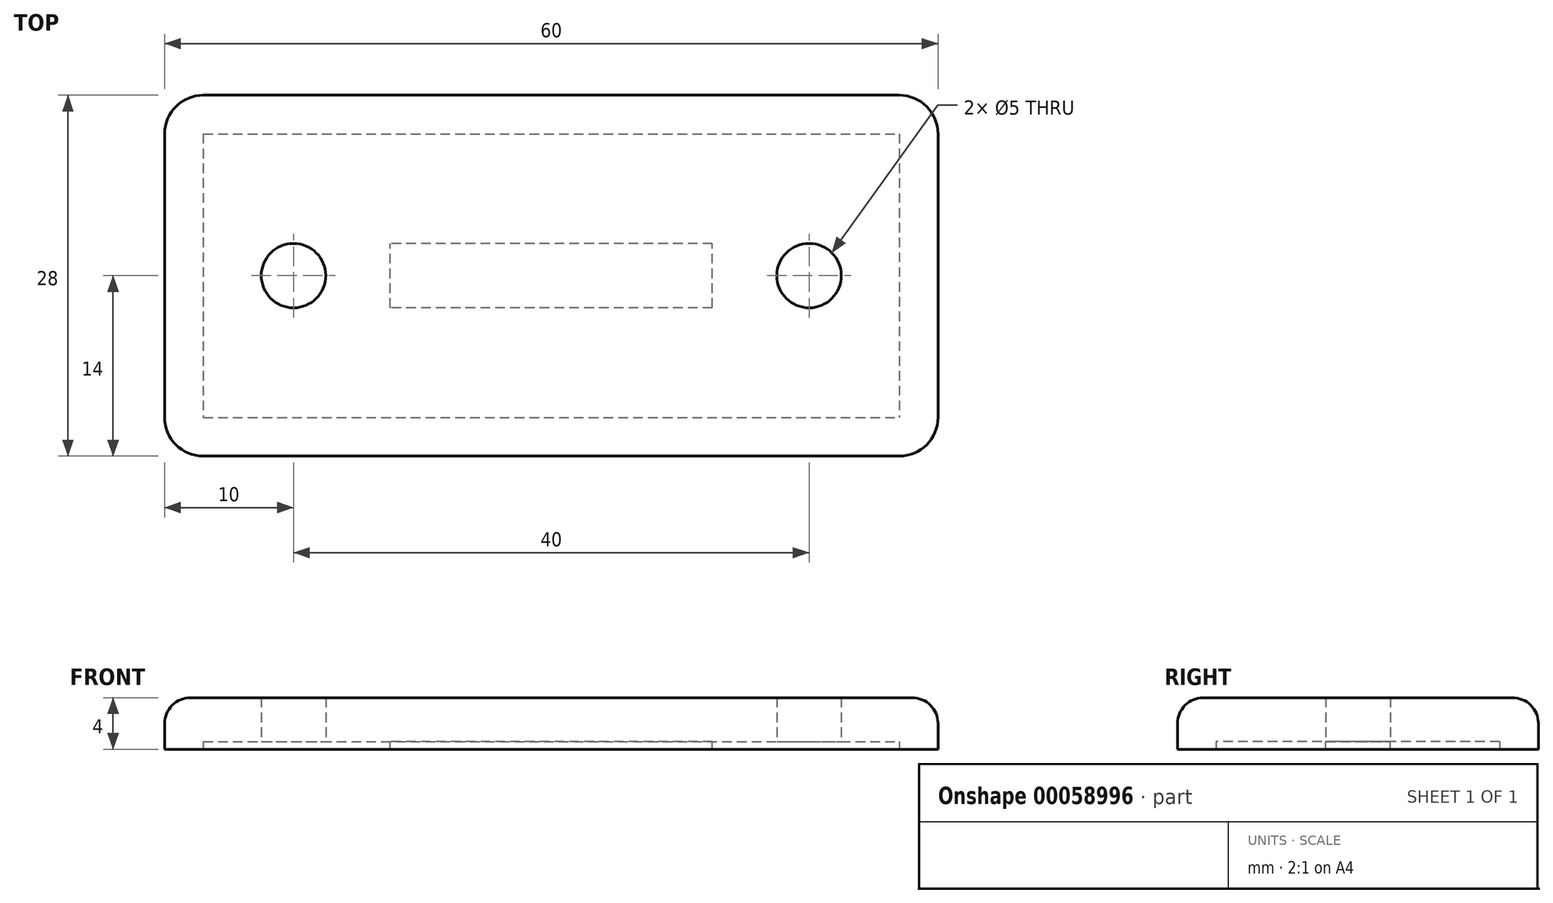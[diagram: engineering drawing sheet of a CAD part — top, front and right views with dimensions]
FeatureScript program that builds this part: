
annotation { "Feature Type Name" : "Feature", "Feature Type Description" : "" }
export const myFeature = defineFeature(function(context is Context, id is Id, definition is map)
    precondition{}
    {
        {
            var Q0;
            Q0=qCreatedBy(makeId("Top.planeOp"),FACE);
            var sketch = newSketch(context, id + "F0", { "sketchPlane" : qUnion([Q0])});
            skLineSegment(sketch, "E0.rect.bottom", {"start": v(-30, 14) * mm, "end": v(30, 14) * mm});
            skLineSegment(sketch, "E0.rect.top", {"start": v(-30, -14) * mm, "end": v(30, -14) * mm});
            skLineSegment(sketch, "E0.rect.left", {"start": v(-30, 14) * mm, "end": v(-30, -14) * mm});
            skLineSegment(sketch, "E0.rect.right", {"start": v(30, 14) * mm, "end": v(30, -14) * mm});
            skPoint(sketch, "E0.rect.middle", {"position": v(0, 0) * mm});
            skCircle(sketch, "E1", {"center": v(-20, 0) * mm, "radius": 2.5 * mm});
            skCircle(sketch, "E2", {"center": v(20, 0) * mm, "radius": 2.5 * mm});
            skSolve(sketch);
        }
        {
            var Q0;
            Q0 = qSketchRegion(id + "F0", true);
            extrude(context, id + "F1", {"entities" : qUnion([Q0]), "depth" : 4 * mm});
        }
        {
            var Q0;
            Q0=makeQuery(id+"F1.opExtrude","CAP_FACE",FACE,{"disambiguationData":[OSD([sQuery(id+"F0.wireOp",EDGE,"E0.rect.bottom"),sQuery(id+"F0.wireOp",EDGE,"E0.rect.top"),sQuery(id+"F0.wireOp",EDGE,"E0.rect.left"),sQuery(id+"F0.wireOp",EDGE,"E0.rect.right"),sQuery(id+"F0.wireOp",EDGE,"E1"),sQuery(id+"F0.wireOp",EDGE,"E2")])],"isStart":true});
            var sketch = newSketch(context, id + "F2", { "sketchPlane" : qUnion([Q0])});
            skLineSegment(sketch, "E3.0", {"start": v(-27, -11) * mm, "end": v(27, -11) * mm});
            skLineSegment(sketch, "E3.1", {"start": v(-27, -11) * mm, "end": v(-27, 11) * mm});
            skLineSegment(sketch, "E3.2", {"start": v(-27, 11) * mm, "end": v(27, 11) * mm});
            skLineSegment(sketch, "E3.3", {"start": v(27, -11) * mm, "end": v(27, 11) * mm});
            skSolve(sketch);
        }
        {
            var Q0;
            Q0 = qSketchRegion(id + "F2", true);
            extrude(context, id + "F3", {"entities" : qUnion([Q0]), "operationType" : NewBodyOperationType.REMOVE, "oppositeDirection" : true, "depth" : 0.6 * mm});
        }
        {
            var Q0;
            Q0=makeQuery(id+"F1.opExtrude","SWEPT_EDGE",EDGE,{"disambiguationData":[OSD([sQuery(id+"F0.wireOp",EDGE,"E0.rect.bottom"),sQuery(id+"F0.wireOp",EDGE,"E0.rect.left")])]});
            var Q1;
            Q1=makeQuery(id+"F1.opExtrude","SWEPT_EDGE",EDGE,{"disambiguationData":[OSD([sQuery(id+"F0.wireOp",EDGE,"E0.rect.top"),sQuery(id+"F0.wireOp",EDGE,"E0.rect.left")])]});
            var Q2;
            Q2=makeQuery(id+"F1.opExtrude","SWEPT_EDGE",EDGE,{"disambiguationData":[OSD([sQuery(id+"F0.wireOp",EDGE,"E0.rect.top"),sQuery(id+"F0.wireOp",EDGE,"E0.rect.right")])]});
            var Q3;
            Q3=makeQuery(id+"F1.opExtrude","SWEPT_EDGE",EDGE,{"disambiguationData":[OSD([sQuery(id+"F0.wireOp",EDGE,"E0.rect.bottom"),sQuery(id+"F0.wireOp",EDGE,"E0.rect.right")])]});
            fillet(context, id + "F4", {"entities" : qUnion([Q0, Q1, Q2, Q3]), "radius" : 3 * mm, "tangentPropagation" : true, "allowEdgeOverflow" : false});
        }
        {
            var Q0;
            Q0=makeQuery(id+"F1.opExtrude","CAP_EDGE",EDGE,{"disambiguationData":[OSD([sQuery(id+"F0.wireOp",EDGE,"E0.rect.bottom")])],"isStart":false});
            fillet(context, id + "F5", {"entities" : qUnion([Q0]), "radius" : 2 * mm, "tangentPropagation" : true, "allowEdgeOverflow" : false});
        }
        {
            var Q0;
            Q0=makeQuery(id+"F3.boolean.opBoolean","COPY",FACE,{"derivedFrom":makeQuery(id+"F3.opExtrude","CAP_FACE",FACE,{"disambiguationData":[OSD([sQuery(id+"F2.wireOp",EDGE,"E3.0"),sQuery(id+"F2.wireOp",EDGE,"E3.1"),sQuery(id+"F2.wireOp",EDGE,"E3.2"),sQuery(id+"F2.wireOp",EDGE,"E3.3")])],"isStart":false})});
            var sketch = newSketch(context, id + "F6", { "sketchPlane" : qUnion([Q0])});
            skLineSegment(sketch, "E4.rect.bottom", {"start": v(12.5, 2.5) * mm, "end": v(-12.5, 2.5) * mm});
            skLineSegment(sketch, "E4.rect.top", {"start": v(12.5, -2.5) * mm, "end": v(-12.5, -2.5) * mm});
            skLineSegment(sketch, "E4.rect.left", {"start": v(12.5, 2.5) * mm, "end": v(12.5, -2.5) * mm});
            skLineSegment(sketch, "E4.rect.right", {"start": v(-12.5, 2.5) * mm, "end": v(-12.5, -2.5) * mm});
            skPoint(sketch, "E4.rect.middle", {"position": v(0, 0) * mm});
            skSolve(sketch);
        }
        {
            var Q0;
            Q0=makeQuery(id+"F6.imprint","IMPRINT",FACE,{"disambiguationData":[TD([[makeQuery(id+"F6.imprint","IMPRINT",EDGE,{"derivedFrom":sQuery(id+"F6.wireOp",EDGE,"E4.rect.bottom")}),1.0]])]});
            var Q1;
            Q1=makeQuery(id+"F1.opExtrude","CAP_FACE",FACE,{"disambiguationData":[OSD([sQuery(id+"F0.wireOp",EDGE,"E0.rect.bottom"),sQuery(id+"F0.wireOp",EDGE,"E0.rect.top"),sQuery(id+"F0.wireOp",EDGE,"E0.rect.left"),sQuery(id+"F0.wireOp",EDGE,"E0.rect.right"),sQuery(id+"F0.wireOp",EDGE,"E1"),sQuery(id+"F0.wireOp",EDGE,"E2")])],"isStart":true});
            extrude(context, id + "F7", {"entities" : qUnion([Q0]), "operationType" : NewBodyOperationType.ADD, "endBound" : BoundingType.UP_TO_SURFACE, "endBoundEntityFace" : qUnion([Q1]), "depth" : 25 * mm});
        }
    });
